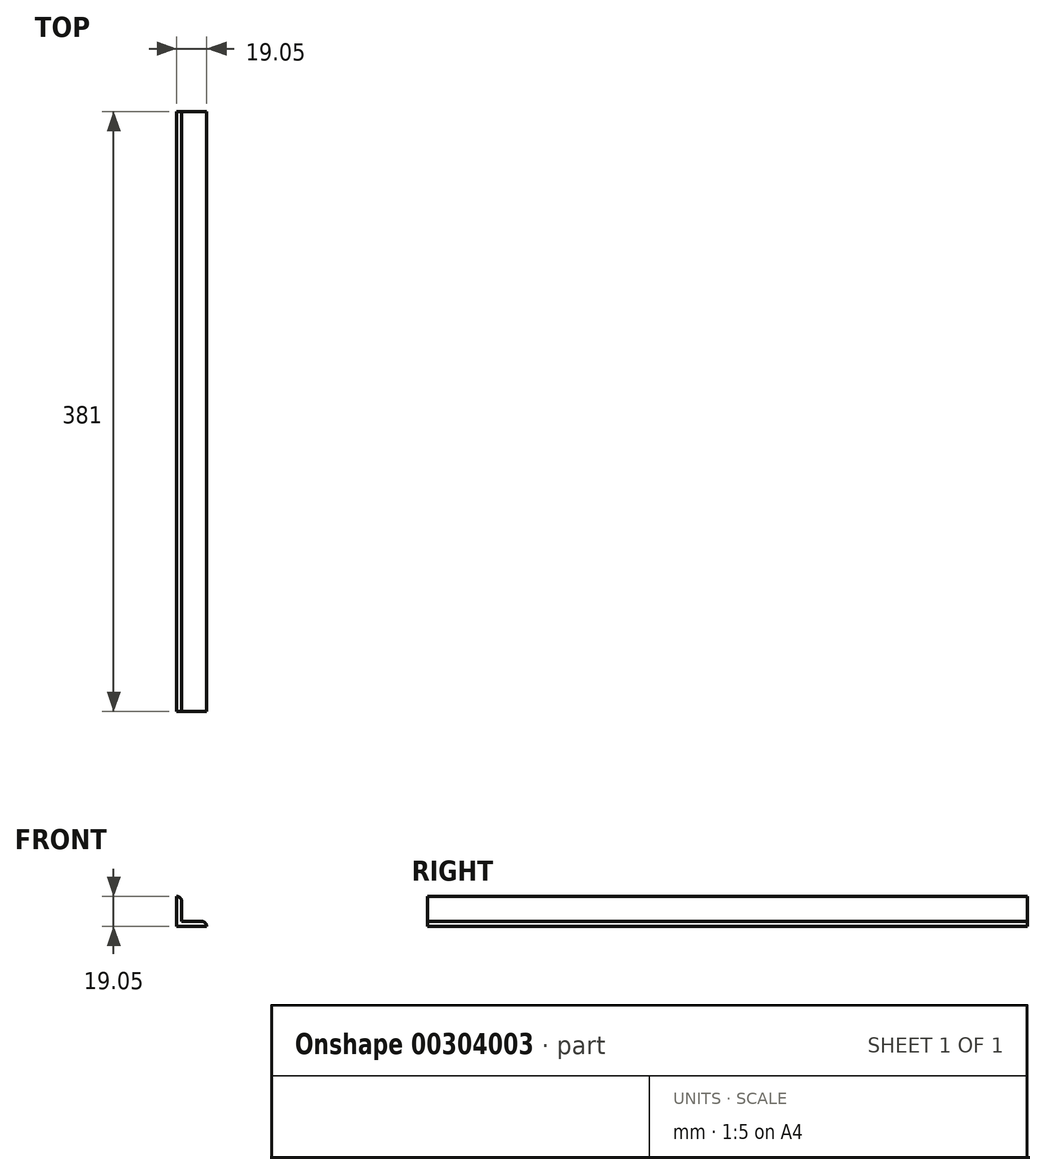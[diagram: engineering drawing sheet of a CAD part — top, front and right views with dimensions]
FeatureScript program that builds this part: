
annotation { "Feature Type Name" : "Feature", "Feature Type Description" : "" }
export const myFeature = defineFeature(function(context is Context, id is Id, definition is map)
    precondition{}
    {
        {
            var Q0;
            Q0=qCreatedBy(makeId("Front.planeOp"),FACE);
            var sketch = newSketch(context, id + "F0", { "sketchPlane" : qUnion([Q0])});
            skLineSegment(sketch, "E0", {"start": v(0, 19.05) * mm, "end": v(0, 0) * mm});
            skLineSegment(sketch, "E1", {"start": v(0, 0) * mm, "end": v(19.05, 0) * mm});
            skLineSegment(sketch, "E2", {"start": v(15.88, 3.17) * mm, "end": v(3.18, 3.17) * mm});
            skLineSegment(sketch, "E3", {"start": v(3.17, 3.17) * mm, "end": v(3.17, 15.88) * mm});
            skLineSegment(sketch, "E4", {"start": v(0, 19.05) * mm, "end": v(0, 19.05) * mm});
            skArc(sketch, "E5.filletArc", {"start": v(3.17, 15.88) * mm, "mid": v(2.25, 18.12) * mm, "end": v(0, 19.05) * mm});
            skArc(sketch, "E6.filletArc", {"start": v(19.05, 0) * mm, "mid": v(18.12, 2.25) * mm, "end": v(15.88, 3.18) * mm});
            skSolve(sketch);
        }
        {
            var Q0;
            Q0 = qSketchRegion(id + "F0", true);
            extrude(context, id + "F1", {"entities" : qUnion([Q0]), "endBound" : BoundingType.SYMMETRIC, "depth" : 381 * mm});
        }
    });
